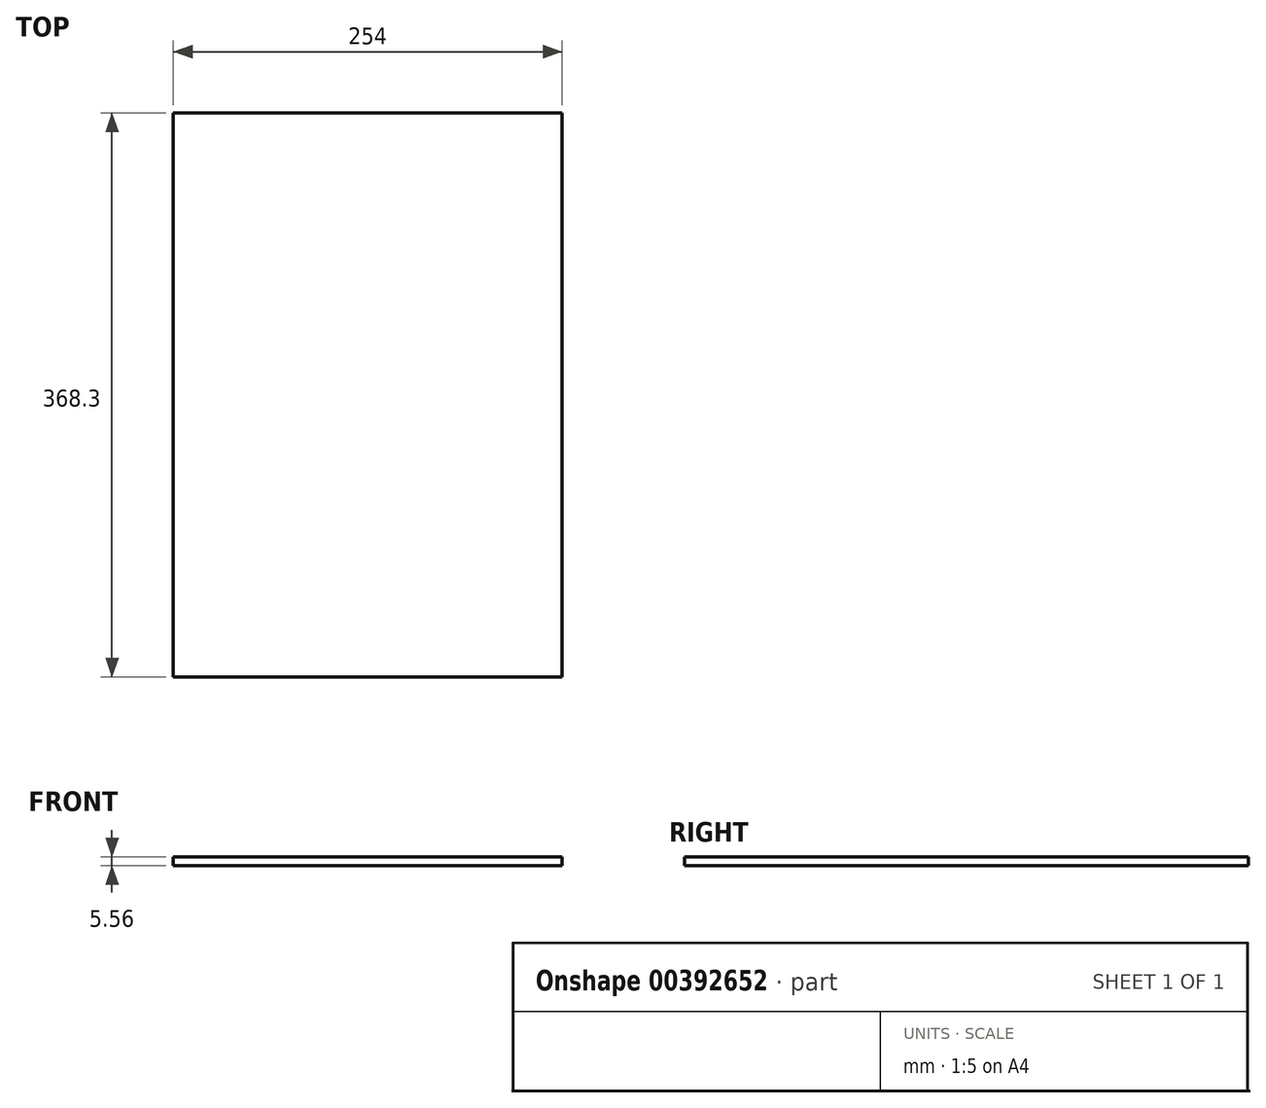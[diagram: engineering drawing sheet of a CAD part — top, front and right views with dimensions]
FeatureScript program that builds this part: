
annotation { "Feature Type Name" : "Feature", "Feature Type Description" : "" }
export const myFeature = defineFeature(function(context is Context, id is Id, definition is map)
    precondition{}
    {
        {
            var Q0;
            Q0=qCreatedBy(makeId("Top.planeOp"),FACE);
            var sketch = newSketch(context, id + "F0", { "sketchPlane" : qUnion([Q0])});
            skLineSegment(sketch, "E0.bottom", {"start": v(0, 0) * mm, "end": v(254, 0) * mm});
            skLineSegment(sketch, "E0.top", {"start": v(0, 368.3) * mm, "end": v(254, 368.3) * mm});
            skLineSegment(sketch, "E0.left", {"start": v(0, 0) * mm, "end": v(0, 368.3) * mm});
            skLineSegment(sketch, "E0.right", {"start": v(254, 0) * mm, "end": v(254, 368.3) * mm});
            skSolve(sketch);
        }
        {
            var Q0;
            Q0=makeQuery(id+"F0.imprint","IMPRINT",FACE,{"disambiguationData":[TD([[makeQuery(id+"F0.imprint","IMPRINT",EDGE,{"derivedFrom":sQuery(id+"F0.wireOp",EDGE,"E0.bottom")}),1.0]])]});
            extrude(context, id + "F1", {"entities" : qUnion([Q0]), "depth" : 5.56 * mm});
        }
    });
